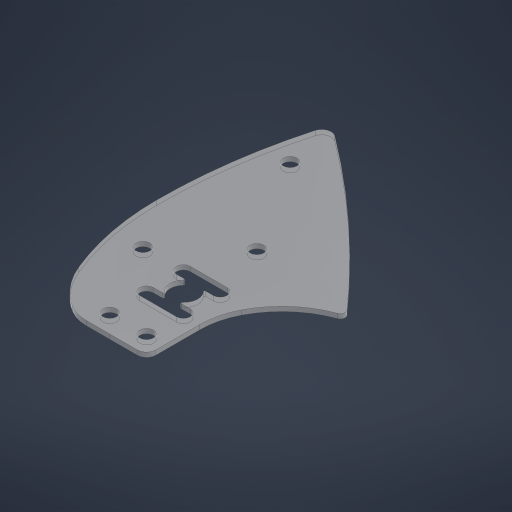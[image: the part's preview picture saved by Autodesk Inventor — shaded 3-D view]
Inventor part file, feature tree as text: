
AUTODESK INVENTOR PART (.ipt)
format: ipt  version: 2024 (Build 280153000, 153)  size: 325,120 bytes
history: native  units: in
note: dims shown in document units (in); Inventor stores cm internally (conversion verified against a paired STEP export)
features: sketch x2, extrude x2, hole x1
ambient origin geometry x8: Origin, YZ Plane, XZ Plane, XY Plane, X Axis, Y Axis, Z Axis, Center Point
bodies: Solid1 (feature_tree)
feature tree (5):
  sketch  "Sketch2"  dims[d3=0.5in d4=1.25in]
  extrude  "Extrusion1"  Depth=0.5in
  hole  "Hole3"  [1 undecoded]
  extrude  "Extrusion2"  Depth=0.0625in TaperAngle=0.0deg
  sketch  "Sketch3"  dims[d5=0.5in d6=0.875in d8=0.0625in d9=0.0in d18=0.125in d19=0.0625in d23=0.185in d24=0.5in d25=1.0in d26=3.0in d27=2.0in d28=0.125in d33=0.25in d35=0.25in d36=0.25in d37=0.25in d38=0.5in d46=0.1875in d47=0.75in d48=0.375in d49=0.25in d50=0.5635in d51=1.0in d52=0.8108in d54=0.25in d55=1.0in d56=2.0in d58=0.75in d59=0.125in d60=0.5in d61=1.25in d62=1.0in d63=0.7518in d64=180.0deg d65=2.0in d66=90.0deg d69=0.055in d70=0.75in d71=90.0deg d72=0.25in d73=0.5in d77=0.375in d78=0.25in d79=0.0104in d80=0.0in d81=0.0in]
note: 1 required parameter value undecoded (feature->parameter linkage not recoverable at this tier; creation-order binding heuristic only, values carry confidence <= 0.55)
